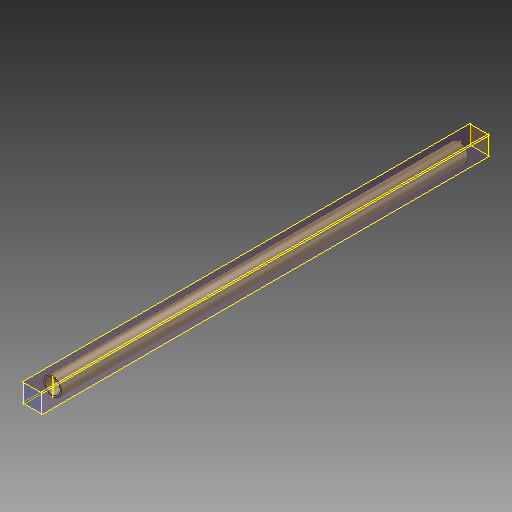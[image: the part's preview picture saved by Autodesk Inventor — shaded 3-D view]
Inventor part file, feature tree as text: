
AUTODESK INVENTOR PART (.ipt)
format: ipt  version: 2018 (Build 220112000, 112)  size: 102,400 bytes
history: native  units: mm
features: other x5, sketch x2, extrude x1
ambient origin geometry x8: Origin, YZ Plane, XZ Plane, XY Plane, X Axis, Y Axis, Z Axis, Center Point
bodies: Body1 (feature_tree)
feature tree (8):
  other  "ソリッド1"
  extrude  "押し出し1"  Depth=27.2mm
  other  "作業平面1"
  other  "作業平面2"
  other  "作業平面3"
  other  "作業平面4"
  sketch  "スケッチ2"
  sketch  "スケッチ1"
